# Revit family: Storage-Freestanding-Teknion-BSLFT_Lateral_File_With_Integral_Worksurface-R2018
name_source: partatom
category: Furniture
revit_build: Autodesk Revit 2018 (Build: 20170223_1515(x64)
units: mm (PartAtom-declared; Revit-internal decimal feet)

## family parameters
Always vertical = Yes
Cut with Voids When Loaded = No
OmniClass Number = 23.40.70.14.64.21
OmniClass Title = Systems Furniture
Room Calculation Point = No
Shared = Yes
Work Plane-Based = No

## types (4) — shared parameters
Assembly Code = E2020200
Manufacturer = Teknion
Manufacturer Fax = 416.661.4586
Part Number = BSLFT
Product Documentation Link = http://www.teknion.com
Product Line = Expansion Casegoods
Product Page URL = https://www.teknion.com
Pull Finish = Mica - Teknion - V - Satin - Very White
Series = Expansion Casegoods
Sustainability Data = http://www.teknion.com
URL = http://www.teknion.com
Unit Weight URL = http://www.teknion.com
Warranty = http://www.teknion.com

## per-type parameters (varying)
| type | Case Finish | Description | Drawer Front Finish | L Finish Configuration | Material Note | Model | T Finish Configuration | U Finish Configuration | W Finish Configuration | Worksurface Finish |
| All Laminate | Source Laminate - Teknion - DE - Latte | Lateral File with Integral Worksurface, All Laminate Finish, 29" Height | Source Laminate - Teknion - DE - Latte | Yes | Case Finish, Drawer Front Finish, and Worksurface Finish must be a Foundation Laminate material. | BSLFT_L__29 | No | No | No | Source Laminate - Teknion - DE - Latte |
| Wood Top, Laminate Front & Case | Source Laminate - Teknion - DE - Latte | Lateral File with Integral Worksurface, Wood Top; Laminate Front & Case, 29" Height | Source Laminate - Teknion - DE - Latte | No | Case Finish and Drawer Front Finish must be Foundation Laminate Material. Worksurface Finish must be a Flintwood material. | BSLFT_T__29 | Yes | No | No | Veneer-Teknion-5U-Flintwood-Raw_Umber (Long Grain) |
| Wood Top & Front, Laminate Case | Source Laminate - Teknion - DE - Latte | Lateral File with Integral Worksurface, Wood Top & Front; Laminate Case, 29" Height | Veneer-Teknion-5U-Flintwood-Raw_Umber (Long Grain) | No | Case Finish must be a Foundation Laminate material. Worksurface Finish and Drawer Front Finish must be a Flintwood material | BSLFT_U__29 | No | Yes | No | Veneer-Teknion-5U-Flintwood-Raw_Umber (Long Grain) |
| All Wood | Veneer-Teknion-5U-Flintwood-Raw_Umber (Long Grain) | Lateral File with Integral Worksurface, All Wood, 29" Height | Veneer-Teknion-5U-Flintwood-Raw_Umber (Long Grain) | No | Case Finish, Drawer Front Finish, and Worksurface Finish must be a Flintwood material. | BSLFT_W__29 | No | No | Yes | Veneer-Teknion-5U-Flintwood-Raw_Umber (Long Grain) |

## geometry (parser evidence)
native form markers: Blend x3, Sweep x2
no freeform markers — native parametric forms only
